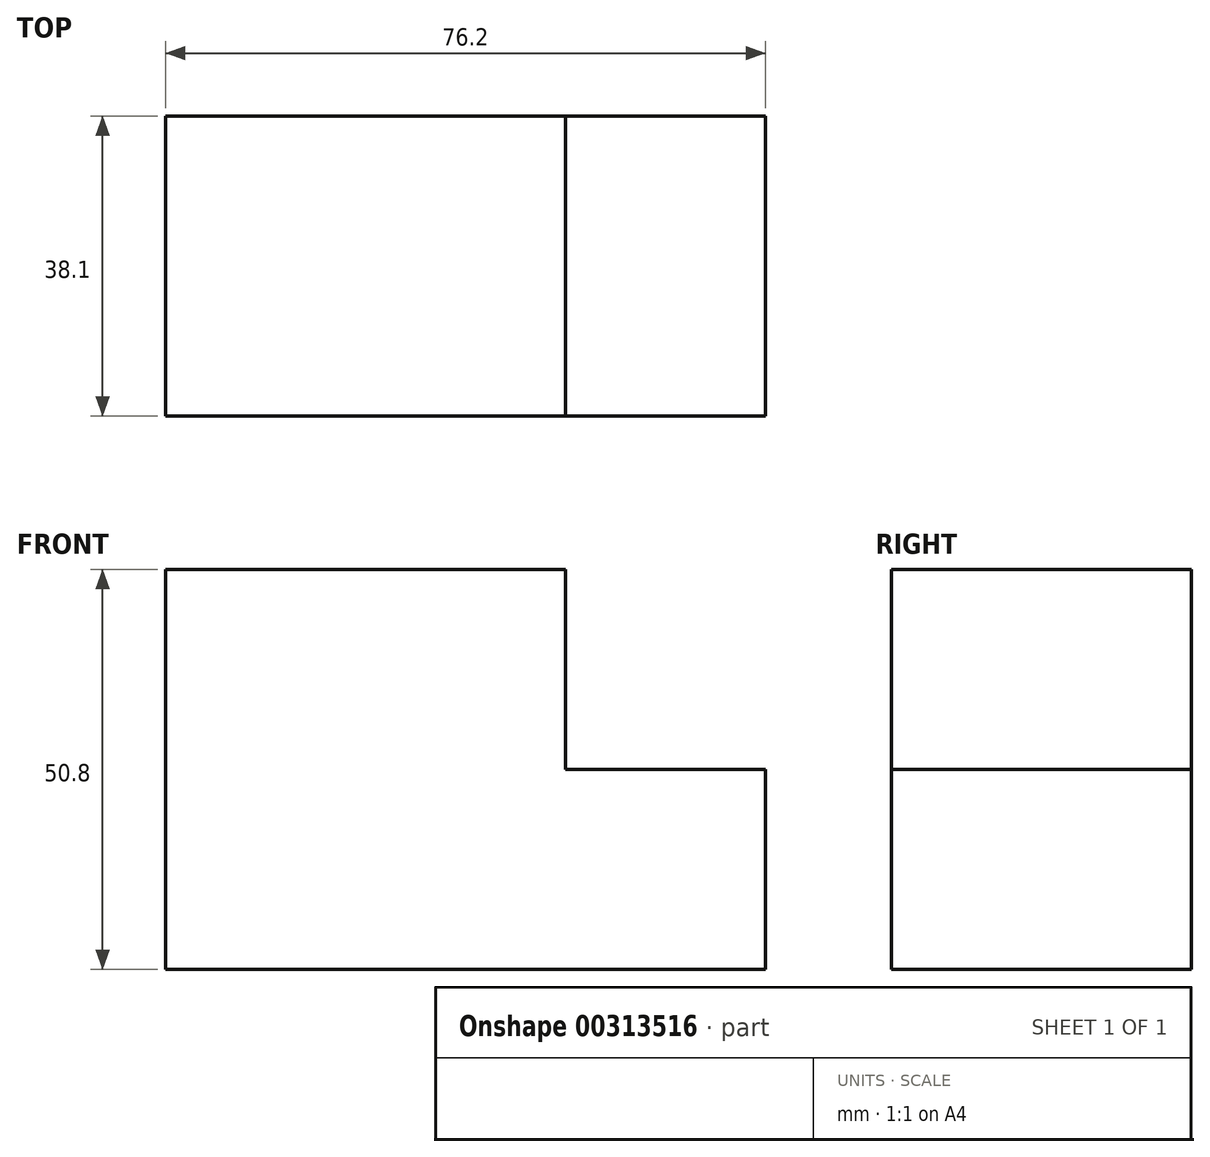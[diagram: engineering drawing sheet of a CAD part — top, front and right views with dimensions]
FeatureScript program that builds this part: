
annotation { "Feature Type Name" : "Feature", "Feature Type Description" : "" }
export const myFeature = defineFeature(function(context is Context, id is Id, definition is map)
    precondition{}
    {
        {
            var Q0;
            Q0=qCreatedBy(makeId("Front.planeOp"),FACE);
            var sketch = newSketch(context, id + "F0", { "sketchPlane" : qUnion([Q0])});
            skLineSegment(sketch, "E0", {"start": v(-38.58, 19.62) * mm, "end": v(-38.58, -31.18) * mm});
            skLineSegment(sketch, "E1", {"start": v(-38.58, -31.18) * mm, "end": v(37.62, -31.18) * mm});
            skLineSegment(sketch, "E2", {"start": v(37.62, -31.18) * mm, "end": v(37.62, -5.78) * mm});
            skLineSegment(sketch, "E3", {"start": v(37.62, -5.78) * mm, "end": v(12.22, -5.78) * mm});
            skLineSegment(sketch, "E4", {"start": v(12.22, -5.78) * mm, "end": v(12.22, 19.62) * mm});
            skLineSegment(sketch, "E5", {"start": v(12.22, 19.62) * mm, "end": v(-38.58, 19.62) * mm});
            skSolve(sketch);
        }
        {
            var Q0;
            Q0=makeQuery(id+"F0.imprint","IMPRINT",FACE,{"disambiguationData":[TD([[makeQuery(id+"F0.imprint","IMPRINT",EDGE,{"derivedFrom":sQuery(id+"F0.wireOp",EDGE,"E0")}),1.0]])]});
            extrude(context, id + "F1", {"entities" : qUnion([Q0]), "depth" : 38.1 * mm});
        }
    });
